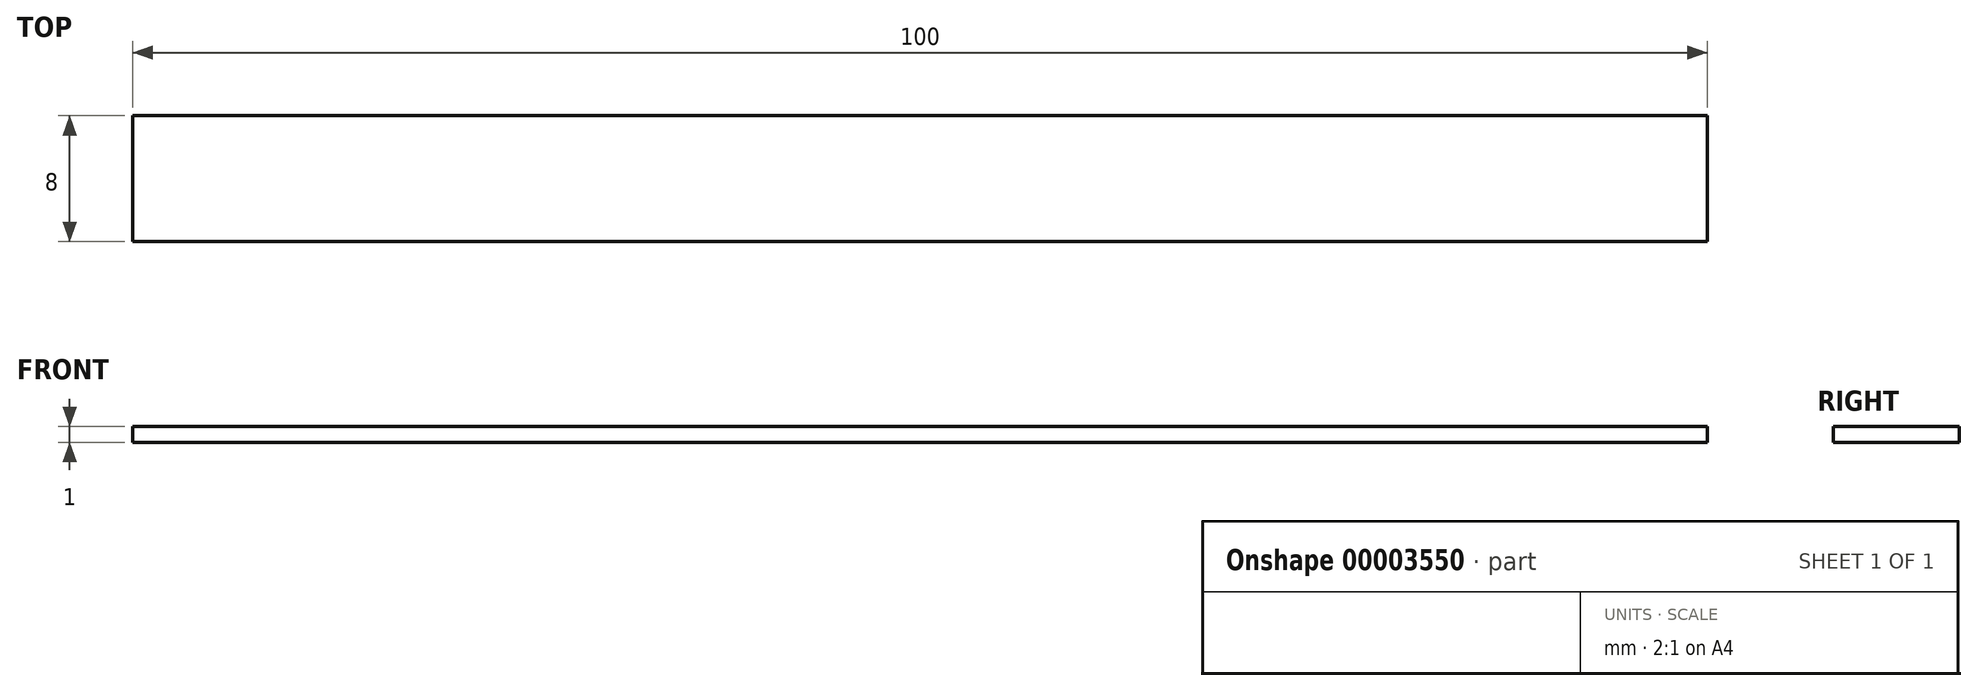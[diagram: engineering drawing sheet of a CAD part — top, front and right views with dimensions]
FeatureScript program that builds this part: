
annotation { "Feature Type Name" : "Feature", "Feature Type Description" : "" }
export const myFeature = defineFeature(function(context is Context, id is Id, definition is map)
    precondition{}
    {
        {
            var Q0;
            Q0=qCreatedBy(makeId("Top.planeOp"),FACE);
            var sketch = newSketch(context, id + "F0", { "sketchPlane" : qUnion([Q0])});
            skLineSegment(sketch, "E0.rect.bottom", {"start": v(50, 4) * mm, "end": v(-50, 4) * mm});
            skLineSegment(sketch, "E0.rect.top", {"start": v(50, -4) * mm, "end": v(-50, -4) * mm});
            skLineSegment(sketch, "E0.rect.left", {"start": v(50, 4) * mm, "end": v(50, -4) * mm});
            skLineSegment(sketch, "E0.rect.right", {"start": v(-50, 4) * mm, "end": v(-50, -4) * mm});
            skPoint(sketch, "E0.rect.middle", {"position": v(0, 0) * mm});
            skSolve(sketch);
        }
        {
            var Q0;
            Q0 = qSketchRegion(id + "F0", true);
            extrude(context, id + "F1", {"entities" : qUnion([Q0]), "depth" : 1 * mm});
        }
    });
